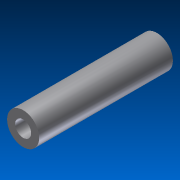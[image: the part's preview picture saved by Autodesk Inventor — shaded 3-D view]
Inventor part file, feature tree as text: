
AUTODESK INVENTOR PART (.ipt)
format: ipt  version: 2012 (Build 160160000, 160)  size: 77,824 bytes
history: native  units: in
note: dims shown in document units (in); Inventor stores cm internally (conversion verified against a paired STEP export)
features: extrude x1, sketch x1
ambient origin geometry x8: Origin, YZ Plane, XZ Plane, XY Plane, X Axis, Y Axis, Z Axis, Center Point
bodies: Solid1 (feature_tree)
feature tree (2):
  extrude  "Extrusion1"  Depth=0.2362in
  sketch  "Sketch1"  dims[d0=0.1181in d1=0.2362in d2=0.9843in d3=0.0in]
